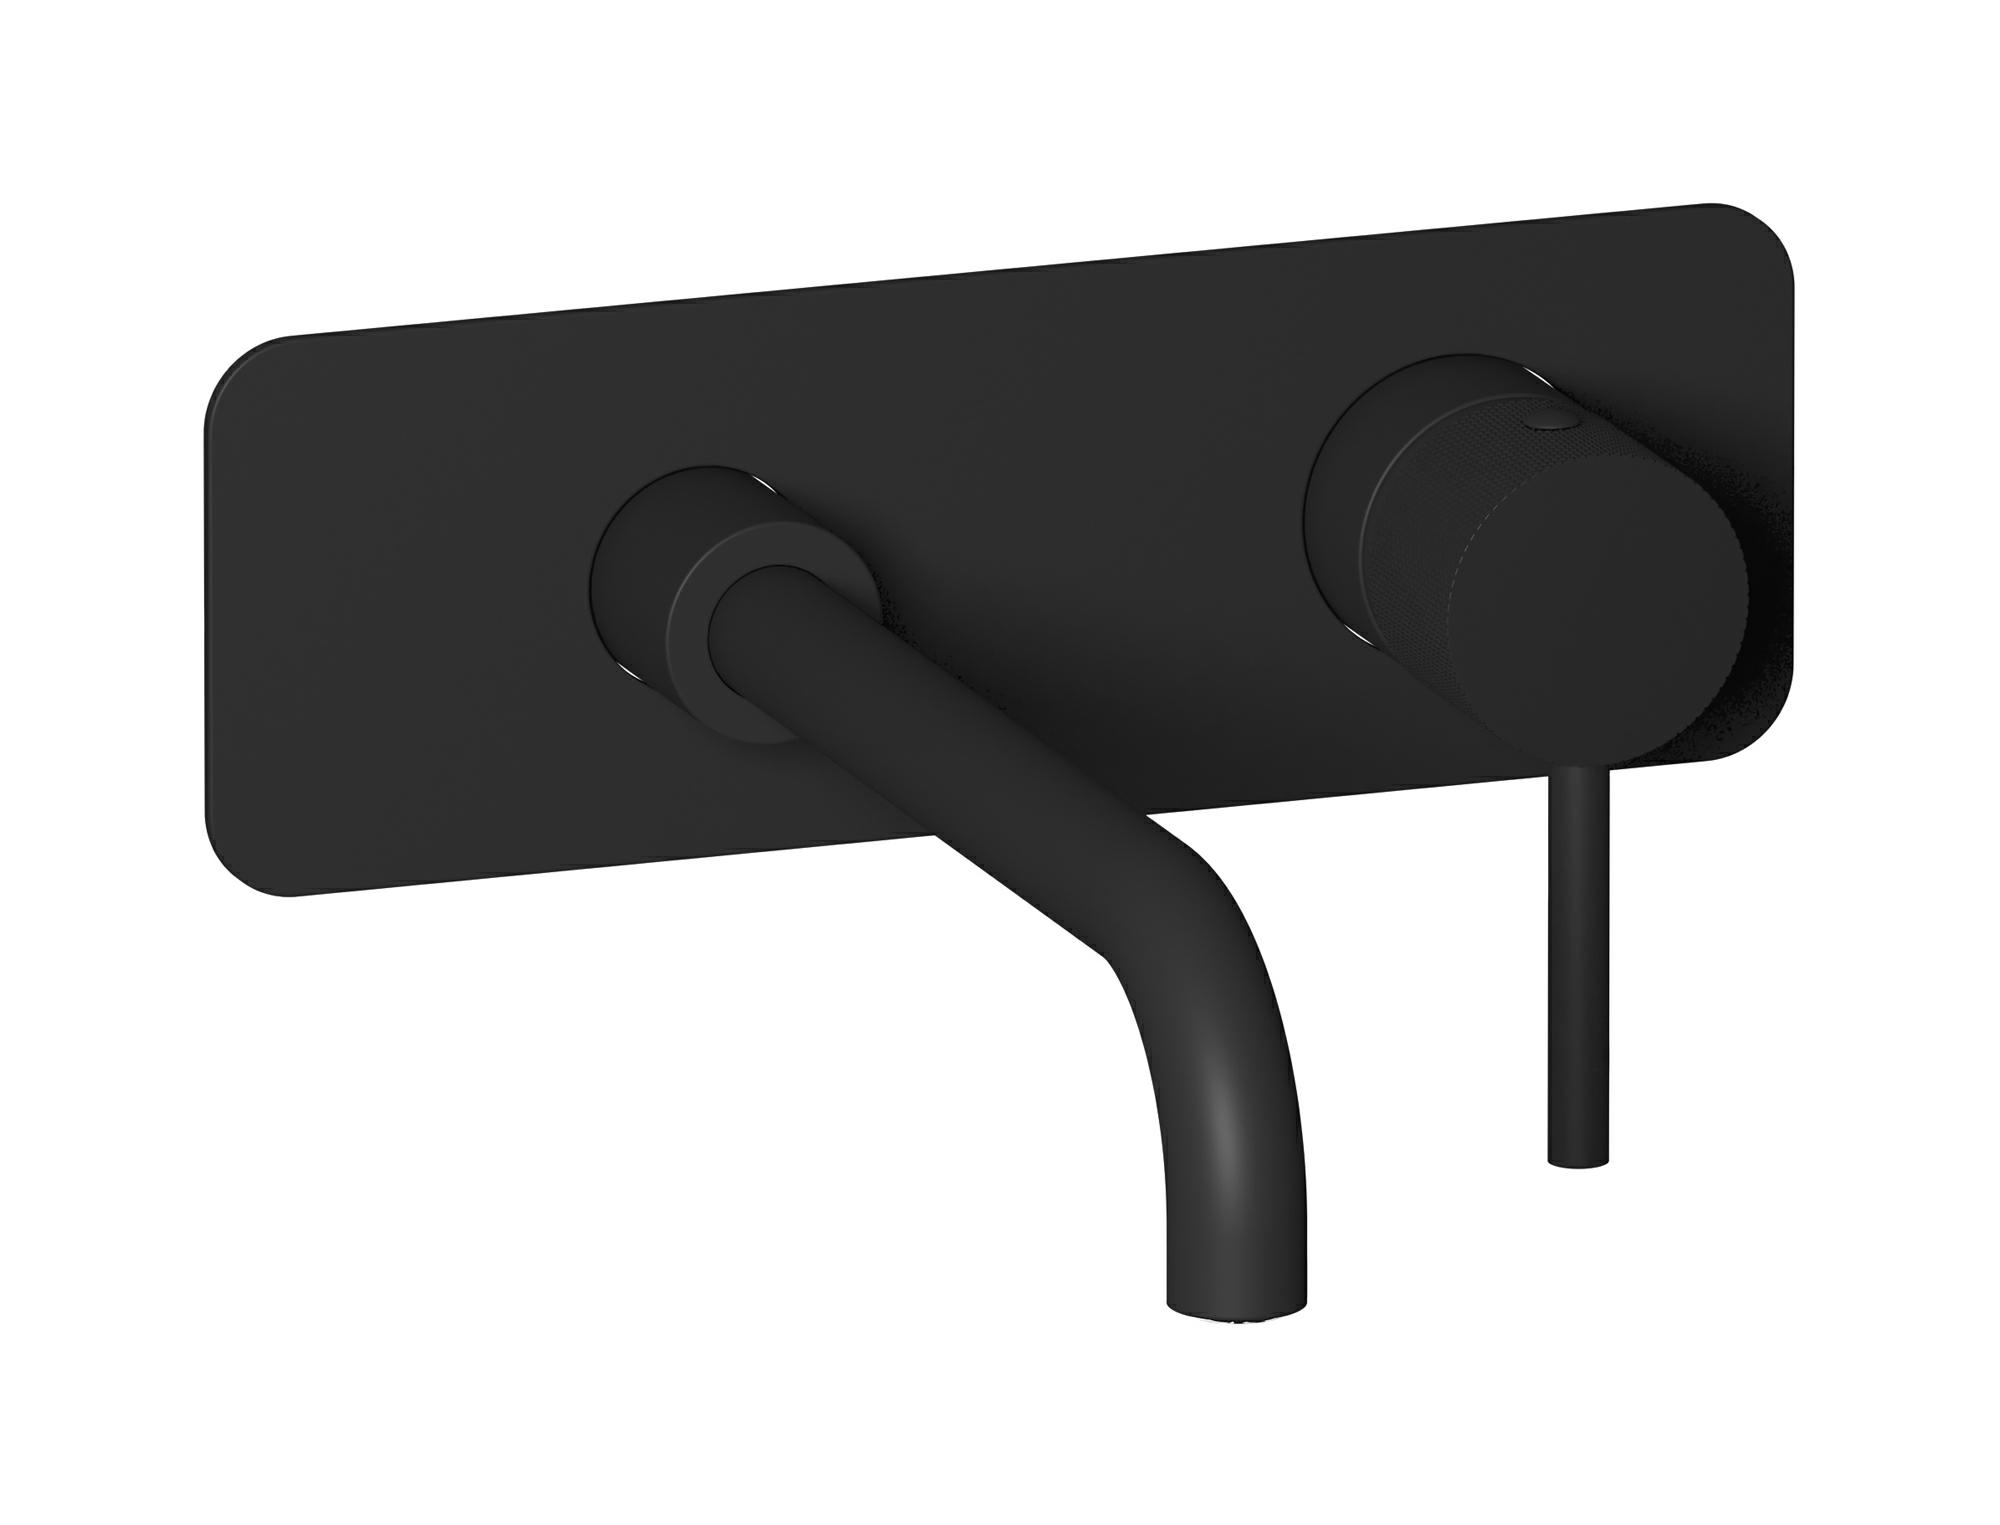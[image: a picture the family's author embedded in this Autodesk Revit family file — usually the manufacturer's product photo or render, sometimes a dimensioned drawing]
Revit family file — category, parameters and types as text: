
# Revit family: ID206
name_source: partatom
category: Apparecchi idraulici
units: mm (PartAtom-declared; Revit-internal decimal feet)

## family parameters
Basato su piano di lavoro = No
Condiviso = No
Mantieni orientamento annotazione = No
Numero OmniClass = 23.45.55.17
Punto di calcolo locali = No
Quota connettore circolare = Usa diametro
Sempre verticale = Sì
Taglio con vuoti quando caricato = No
Tipo di parte = Normale
Titolo OmniClass = Mixing Faucets

## types (12) — shared parameters
Cold water inlet = 10 mm  [stored 0.0328084 ft]
Commenti sul tipo = Washbasin mixer
Connessione CW = No
Connessione HW = No
Connessione di scarico = No
Connessione di ventilazione = No
Descrizione = Wall mounted washbasin mixer complete with drain
Hot water inlet = 10 mm  [stored 0.0328084 ft]
Produttore = IB Rubinetterie S.p.A.
URL = https://www.weareib.it
zero-valued in all types: Prospetto di default

## per-type parameters (varying)
| type | Finishes surface | Immagine tipo | Modello |
| Chrome | IB_Chrome | ID206CC.jpg | ID206CC |
| Brushed nickel | IB_Brushed nickel | ID206SS.jpg | ID206SS |
| Natural brass | IB_Brass | ID206ON.jpg | ID206ON |
| Matt black | IB_matt black | ID206NP.jpg | ID206NP |
| Black chrome | IB_Black chrome | ID206CF.jpg | ID206CF |
| Brushed black chrome | IB_Brushed black chrome | ID206CS.jpg | ID206CS |
| Pale gold | IB_Pale gold | ID206II.jpg | ID206II |
| Brushed pale gold | IB_brushed pale gold | ID206IS.jpg | ID206IS |
| Rose gold | IB_Rose gold | ID206RS.jpg | ID206RS |
| Brushed rose gold | IB_Brushed rose gold | ID206SR.jpg | ID206SR |
| Gold | IB_gold | ID206OO.jpg | ID206OO |
| Brushed gold | IB_brushed gold | ID206OS.jpg | ID206OS |

note: [stored X ft] marks values corroborated as IEEE doubles in the binary element streams (Revit-internal decimal feet)
